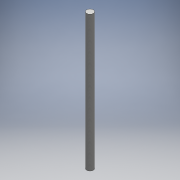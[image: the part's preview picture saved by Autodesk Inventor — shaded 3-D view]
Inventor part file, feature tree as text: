
AUTODESK INVENTOR PART (.ipt)
format: ipt  version: 2018 (Build 220112000, 112)  size: 92,160 bytes
history: native  units: mm
features: other x1, extrude x1, thread x1, sketch x1
ambient origin geometry x8: Origin, YZ Plane, XZ Plane, XY Plane, X Axis, Y Axis, Z Axis, Center Point
bodies: Body1 (feature_tree)
feature tree (4):
  other  "ソリッド1"
  extrude  "押し出し1"  Depth=12.0mm
  thread  "ねじ1"
  sketch  "スケッチ1"
